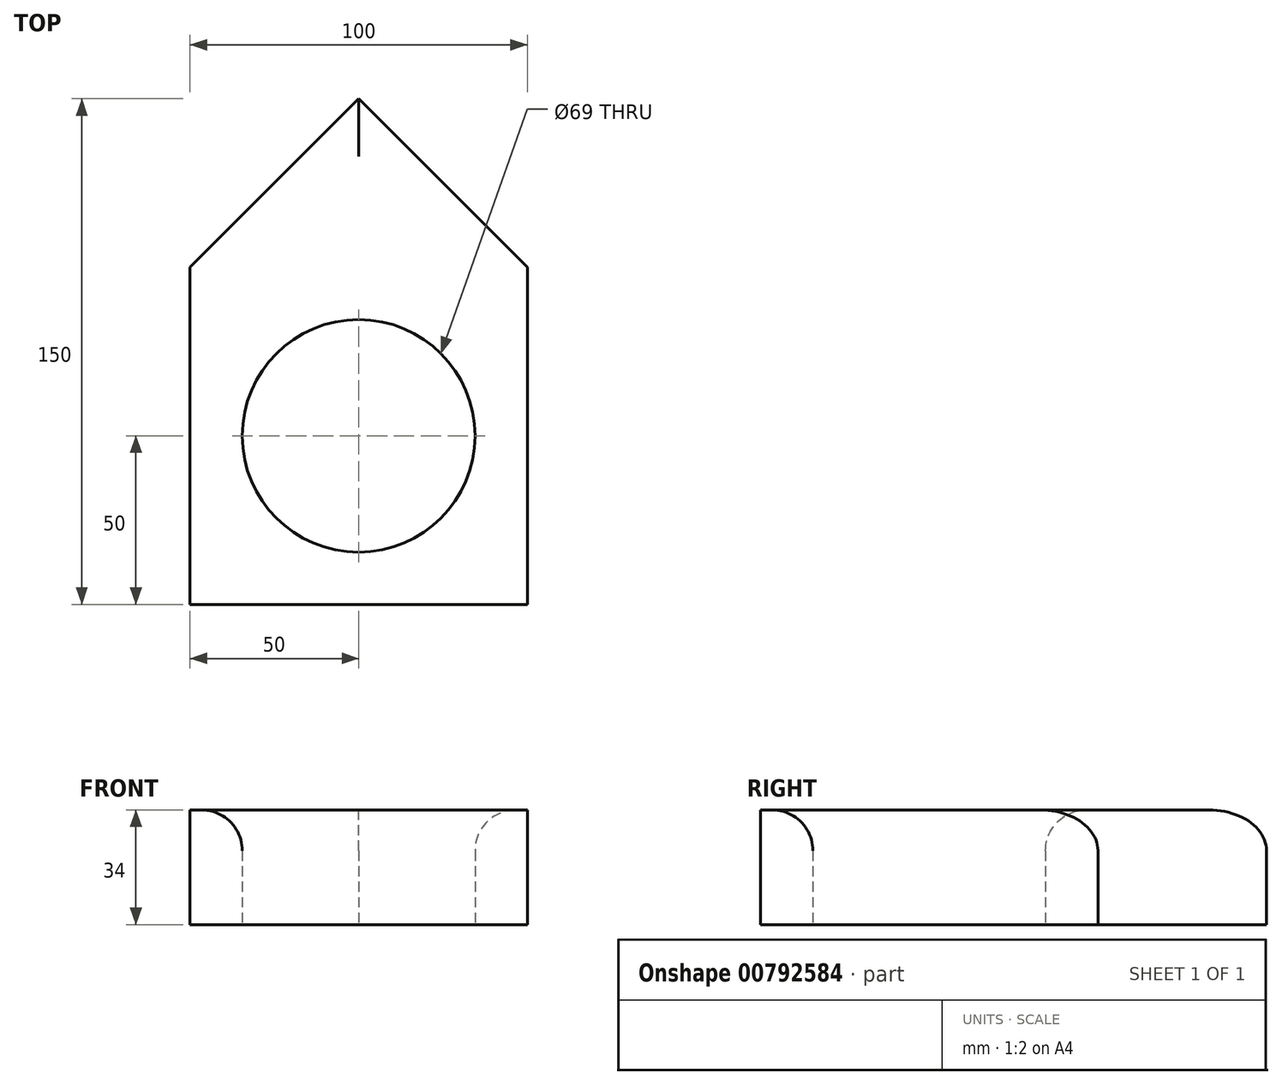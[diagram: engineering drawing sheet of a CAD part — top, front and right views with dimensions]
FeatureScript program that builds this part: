
annotation { "Feature Type Name" : "Feature", "Feature Type Description" : "" }
export const myFeature = defineFeature(function(context is Context, id is Id, definition is map)
    precondition{}
    {
        {
            var Q0;
            Q0=qCreatedBy(makeId("Top.planeOp"),FACE);
            var sketch = newSketch(context, id + "F0", { "sketchPlane" : qUnion([Q0])});
            skLineSegment(sketch, "E0.bottom", {"start": v(-50, 50) * mm, "end": v(50, 50) * mm});
            skLineSegment(sketch, "E0.top", {"start": v(-50, -50) * mm, "end": v(50, -50) * mm});
            skLineSegment(sketch, "E0.left", {"start": v(-50, 50) * mm, "end": v(-50, -50) * mm});
            skLineSegment(sketch, "E0.right", {"start": v(50, 50) * mm, "end": v(50, -50) * mm});
            skCircle(sketch, "E1", {"center": v(0, 0) * mm, "radius": 34.5 * mm});
            skLineSegment(sketch, "E2", {"start": v(-50, 50) * mm, "end": v(0, 100) * mm});
            skLineSegment(sketch, "E3", {"start": v(0, 100) * mm, "end": v(50, 50) * mm});
            skLineSegment(sketch, "E4", {"start": v(-50, 50) * mm, "end": v(50, -50) * mm, "construction": true});
            skSolve(sketch);
        }
        {
            var Q0;
            Q0=makeQuery(id+"F0.imprint","IMPRINT",FACE,{"disambiguationData":[TD([[makeQuery(id+"F0.imprint","IMPRINT",EDGE,{"derivedFrom":sQuery(id+"F0.wireOp",EDGE,"E0.bottom")}),-1.0]])]});
            var Q1;
            Q1=makeQuery(id+"F0.imprint","IMPRINT",FACE,{"disambiguationData":[TD([[makeQuery(id+"F0.imprint","IMPRINT",EDGE,{"derivedFrom":sQuery(id+"F0.wireOp",EDGE,"E0.bottom")}),1.0]])]});
            extrude(context, id + "F1", {"entities" : qUnion([Q0, Q1]), "depth" : 34 * mm, "offsetDistance" : 25 * mm});
        }
        {
            var Q0;
            Q0=makeQuery(id+"F1.opExtrude","CAP_EDGE",EDGE,{"disambiguationData":[OSD([sQuery(id+"F0.wireOp",EDGE,"E1")])],"isStart":false});
            var Q1;
            Q1=makeQuery(id+"F1.opExtrude","CAP_EDGE",EDGE,{"disambiguationData":[OSD([sQuery(id+"F0.wireOp",EDGE,"E3")])],"isStart":false});
            var Q2;
            Q2=makeQuery(id+"F1.opExtrude","CAP_EDGE",EDGE,{"disambiguationData":[OSD([sQuery(id+"F0.wireOp",EDGE,"E2")])],"isStart":false});
            fillet(context, id + "F2", {"entities" : qUnion([Q0, Q1, Q2]), "radius" : 12.07 * mm, "tangentPropagation" : true, "allowEdgeOverflow" : false});
        }
    });
